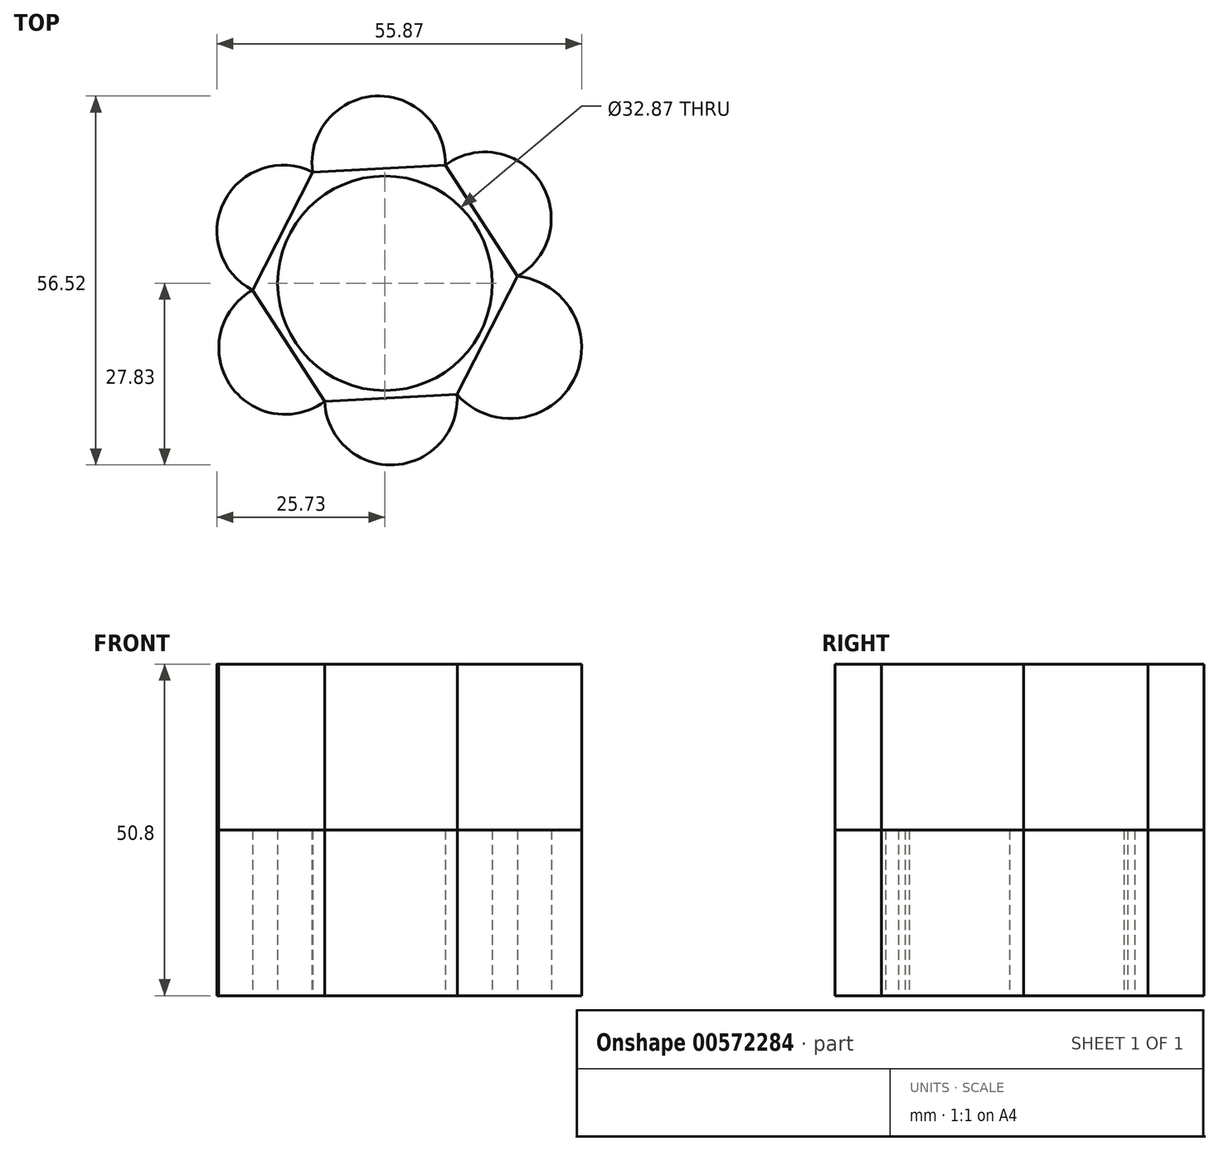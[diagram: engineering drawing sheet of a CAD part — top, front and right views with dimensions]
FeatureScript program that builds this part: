
annotation { "Feature Type Name" : "Feature", "Feature Type Description" : "" }
export const myFeature = defineFeature(function(context is Context, id is Id, definition is map)
    precondition{}
    {
        {
            var Q0;
            Q0=qCreatedBy(makeId("Top.planeOp"),FACE);
            var sketch = newSketch(context, id + "F0", { "sketchPlane" : qUnion([Q0])});
            skCircle(sketch, "E0.cCircle", {"center": v(0, 0) * mm, "radius": 17.6 * mm, "construction": true});
            skLineSegment(sketch, "E0.0", {"start": v(20.3, 1.06) * mm, "end": v(11.06, -17.05) * mm});
            skLineSegment(sketch, "E0.1", {"start": v(11.06, -17.05) * mm, "end": v(-9.23, -18.1) * mm});
            skLineSegment(sketch, "E0.2", {"start": v(-9.23, -18.1) * mm, "end": v(-20.3, -1.06) * mm});
            skLineSegment(sketch, "E0.3", {"start": v(-20.3, -1.06) * mm, "end": v(-11.06, 17.05) * mm});
            skLineSegment(sketch, "E0.4", {"start": v(-11.06, 17.05) * mm, "end": v(9.23, 18.1) * mm});
            skLineSegment(sketch, "E0.5", {"start": v(9.23, 18.1) * mm, "end": v(20.3, 1.06) * mm});
            skPoint(sketch, "E0.0.midPoint", {"position": v(15.68, -8) * mm});
            skArc(sketch, "E1", {"start": v(9.23, 18.1) * mm, "mid": v(-1.5, 28.68) * mm, "end": v(-11.06, 17.05) * mm});
            skArc(sketch, "E2", {"start": v(11.06, -17.05) * mm, "mid": v(28.95, -14.77) * mm, "end": v(20.3, 1.06) * mm});
            skArc(sketch, "E3", {"start": v(-20.3, -1.06) * mm, "mid": v(-23.81, -15.45) * mm, "end": v(-9.23, -18.1) * mm});
            skArc(sketch, "E4", {"start": v(-11.06, 17.05) * mm, "mid": v(-24.62, 12.56) * mm, "end": v(-20.3, -1.06) * mm});
            skArc(sketch, "E5", {"start": v(-9.23, -18.1) * mm, "mid": v(1.45, -27.82) * mm, "end": v(11.06, -17.05) * mm});
            skArc(sketch, "E6", {"start": v(20.3, 1.06) * mm, "mid": v(23.84, 15.47) * mm, "end": v(9.23, 18.1) * mm});
            skSolve(sketch);
        }
        {
            var Q0;
            Q0=makeQuery(id+"F0.imprint","IMPRINT",FACE,{"disambiguationData":[TD([[makeQuery(id+"F0.imprint","IMPRINT",EDGE,{"derivedFrom":sQuery(id+"F0.wireOp",EDGE,"E0.4")}),1.0]])]});
            var Q1;
            Q1=makeQuery(id+"F0.imprint","IMPRINT",FACE,{"disambiguationData":[TD([[makeQuery(id+"F0.imprint","IMPRINT",EDGE,{"derivedFrom":sQuery(id+"F0.wireOp",EDGE,"E0.3")}),1.0]])]});
            var Q2;
            Q2=makeQuery(id+"F0.imprint","IMPRINT",FACE,{"disambiguationData":[TD([[makeQuery(id+"F0.imprint","IMPRINT",EDGE,{"derivedFrom":sQuery(id+"F0.wireOp",EDGE,"E0.2")}),1.0]])]});
            var Q3;
            Q3=makeQuery(id+"F0.imprint","IMPRINT",FACE,{"disambiguationData":[TD([[makeQuery(id+"F0.imprint","IMPRINT",EDGE,{"derivedFrom":sQuery(id+"F0.wireOp",EDGE,"E0.1")}),1.0]])]});
            var Q4;
            Q4=makeQuery(id+"F0.imprint","IMPRINT",FACE,{"disambiguationData":[TD([[makeQuery(id+"F0.imprint","IMPRINT",EDGE,{"derivedFrom":sQuery(id+"F0.wireOp",EDGE,"E0.0")}),1.0]])]});
            var Q5;
            Q5=makeQuery(id+"F0.imprint","IMPRINT",FACE,{"disambiguationData":[TD([[makeQuery(id+"F0.imprint","IMPRINT",EDGE,{"derivedFrom":sQuery(id+"F0.wireOp",EDGE,"E0.5")}),1.0]])]});
            extrude(context, id + "F1", {"entities" : qUnion([Q0, Q1, Q2, Q3, Q4, Q5]), "depth" : 50.8 * mm, "offsetDistance" : 25.4 * mm});
        }
        {
            var Q0;
            Q0 = qSketchRegion(id + "F0", true);
            extrude(context, id + "F2", {"entities" : qUnion([Q0]), "depth" : 25.4 * mm, "offsetDistance" : 25.4 * mm});
        }
        {
            var Q0;
            Q0=qCreatedBy(makeId("Top.planeOp"),FACE);
            var sketch = newSketch(context, id + "F3", { "sketchPlane" : qUnion([Q0])});
            skCircle(sketch, "E7", {"center": v(0, 0) * mm, "radius": 16.44 * mm});
            skSolve(sketch);
        }
        {
            var Q0;
            Q0 = qSketchRegion(id + "F3", true);
            extrude(context, id + "F4", {"entities" : qUnion([Q0]), "operationType" : NewBodyOperationType.REMOVE, "depth" : 50.8 * mm, "offsetDistance" : 25.4 * mm});
        }
    });
